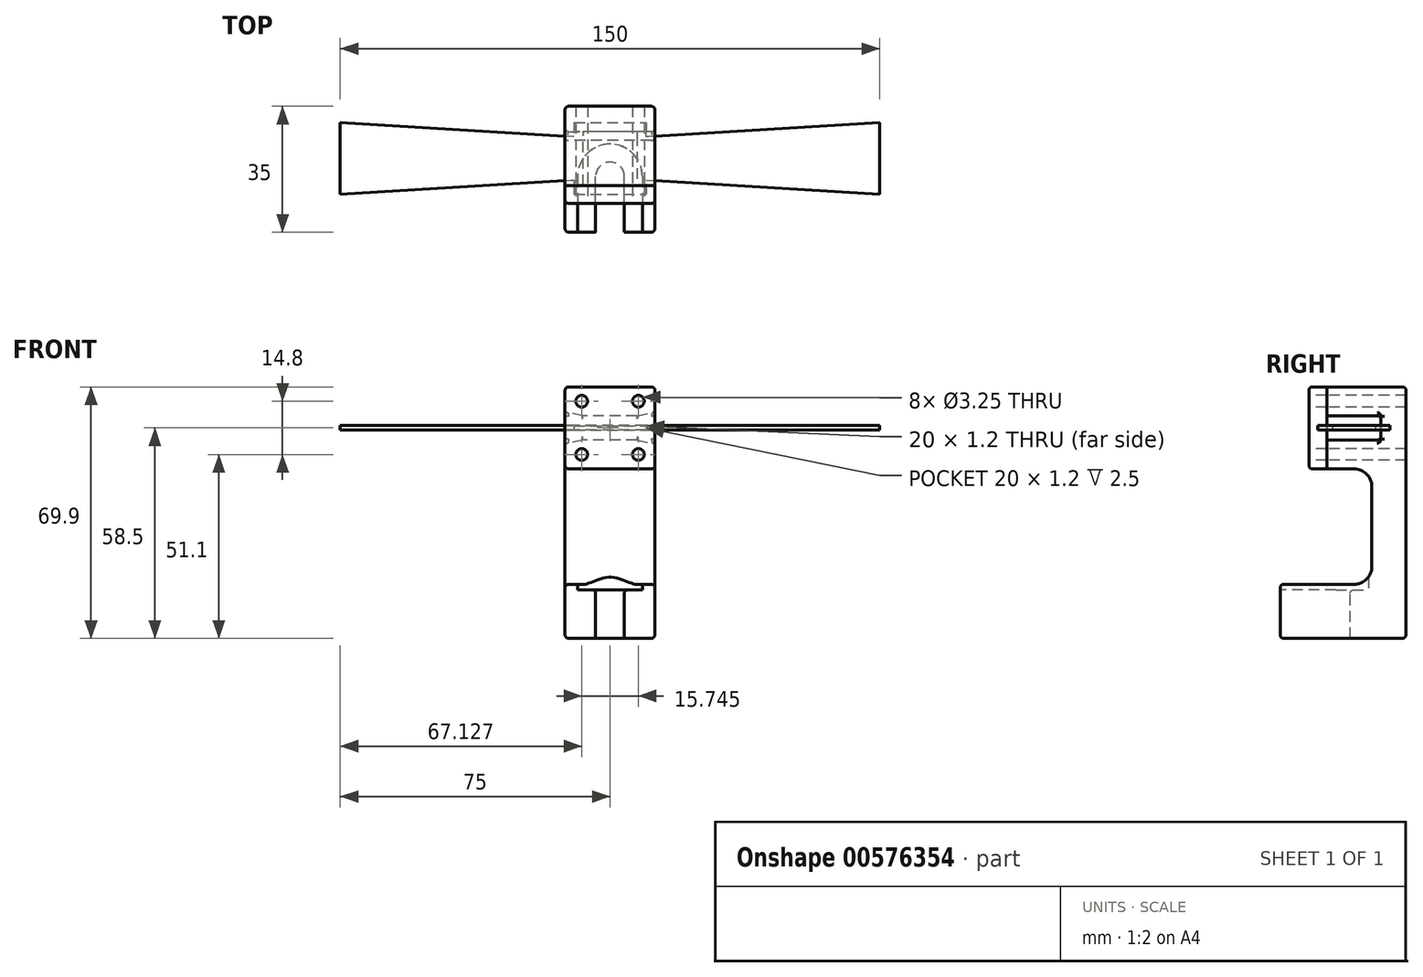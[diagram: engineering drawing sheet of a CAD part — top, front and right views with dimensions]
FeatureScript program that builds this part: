
annotation { "Feature Type Name" : "Feature", "Feature Type Description" : "" }
export const myFeature = defineFeature(function(context is Context, id is Id, definition is map)
    precondition{}
    {
        {
            var Q0;
            Q0=qCreatedBy(makeId("Top.planeOp"),FACE);
            var sketch = newSketch(context, id + "F0", { "sketchPlane" : qUnion([Q0])});
            skLineSegment(sketch, "E0", {"start": v(-142.1, 7.82) * mm, "end": v(142.1, -7.82) * mm, "construction": true});
            skLineSegment(sketch, "E1", {"start": v(-142.1, 0) * mm, "end": v(142.1, 0) * mm, "construction": true});
            skLineSegment(sketch, "E2", {"start": v(-142.1, -7.82) * mm, "end": v(142.1, 7.82) * mm, "construction": true});
            skLineSegment(sketch, "E3", {"start": v(-109.15, 10.59) * mm, "end": v(0, 4.58) * mm});
            skLineSegment(sketch, "E4", {"start": v(-109.15, 1.42) * mm, "end": v(-83.26, 0) * mm});
            skLineSegment(sketch, "E5", {"start": v(-109.15, -10.59) * mm, "end": v(0, -4.58) * mm});
            skLineSegment(sketch, "E6", {"start": v(109.15, 10.59) * mm, "end": v(0, 4.58) * mm});
            skLineSegment(sketch, "E7", {"start": v(0, 26.52) * mm, "end": v(0, -30.87) * mm, "construction": true});
            skLineSegment(sketch, "E8.trimOffspring", {"start": v(-83.26, 0) * mm, "end": v(-109.15, -1.42) * mm});
            skLineSegment(sketch, "E9.trimOffspring", {"start": v(0, -4.58) * mm, "end": v(109.15, -10.59) * mm});
            skLineSegment(sketch, "E10.trimOffspring", {"start": v(83.26, 0) * mm, "end": v(109.15, 1.42) * mm});
            skLineSegment(sketch, "E11.trimOffspring", {"start": v(83.26, 0) * mm, "end": v(109.15, -1.42) * mm});
            skLineSegment(sketch, "E12", {"start": v(109.15, 10.59) * mm, "end": v(109.15, 1.42) * mm});
            skLineSegment(sketch, "E13", {"start": v(109.15, -1.42) * mm, "end": v(109.15, -10.59) * mm});
            skLineSegment(sketch, "E14", {"start": v(-109.15, 10.59) * mm, "end": v(-109.15, 1.42) * mm});
            skLineSegment(sketch, "E15", {"start": v(-109.15, -1.42) * mm, "end": v(-109.15, -10.59) * mm});
            skSolve(sketch);
        }
        {
            var Q0;
            Q0=qCreatedBy(makeId("Right.planeOp"),FACE);
            var sketch = newSketch(context, id + "F1", { "sketchPlane" : qUnion([Q0])});
            skLineSegment(sketch, "E16", {"start": v(14.5, -58.5) * mm, "end": v(-20.5, -58.5) * mm});
            skLineSegment(sketch, "E17", {"start": v(14.5, 11.4) * mm, "end": v(-7.5, 11.4) * mm});
            skLineSegment(sketch, "E18", {"start": v(0, 18.84) * mm, "end": v(0, -56.33) * mm, "construction": true});
            skLineSegment(sketch, "E19.bottom", {"start": v(-7.5, 3.4) * mm, "end": v(7.5, 3.4) * mm});
            skLineSegment(sketch, "E19.right", {"start": v(7.5, 3.4) * mm, "end": v(7.5, -3.4) * mm});
            skLineSegment(sketch, "E20.top", {"start": v(-7.5, -3.4) * mm, "end": v(7.5, -3.4) * mm});
            skLineSegment(sketch, "E21", {"start": v(-7.5, -11.4) * mm, "end": v(5, -11.4) * mm});
            skLineSegment(sketch, "E22", {"start": v(5, -11.4) * mm, "end": v(5, -43.5) * mm});
            skLineSegment(sketch, "E23", {"start": v(5, -43.5) * mm, "end": v(-20.5, -43.5) * mm});
            skLineSegment(sketch, "E24.trimOffspring", {"start": v(-20.5, -43.5) * mm, "end": v(-20.5, -58.5) * mm});
            skLineSegment(sketch, "E25", {"start": v(14.5, 11.4) * mm, "end": v(14.5, -58.5) * mm});
            skLineSegment(sketch, "E26", {"start": v(-7.5, 11.4) * mm, "end": v(-7.5, 3.4) * mm});
            skLineSegment(sketch, "E27", {"start": v(-7.5, -3.4) * mm, "end": v(-7.5, -11.4) * mm});
            skLineSegment(sketch, "E28", {"start": v(-5, -34.47) * mm, "end": v(-5, -58.14) * mm, "construction": true});
            skSolve(sketch);
        }
        {
            var Q0;
            Q0 = qSketchRegion(id + "F1", true);
            extrude(context, id + "F2", {"entities" : qUnion([Q0]), "depth" : 25 * mm, "offsetDistance" : 25 * mm, "symmetric" : true});
        }
        {
            var Q0;
            Q0=makeQuery(id+"F2.opExtrude","SWEPT_FACE",FACE,{"disambiguationData":[OSD([sQuery(id+"F1.wireOp",EDGE,"E26")])]});
            var sketch = newSketch(context, id + "F3", { "sketchPlane" : qUnion([Q0])});
            skCircle(sketch, "E29", {"center": v(-7.87, 7.4) * mm, "radius": 1.25 * mm});
            skCircle(sketch, "E30", {"center": v(7.87, 7.4) * mm, "radius": 1.25 * mm});
            skCircle(sketch, "E31", {"center": v(-7.87, -7.4) * mm, "radius": 1.25 * mm});
            skCircle(sketch, "E32", {"center": v(7.87, -7.4) * mm, "radius": 1.25 * mm});
            skSolve(sketch);
        }
        {
            var Q0;
            Q0 = qSketchRegion(id + "F3", true);
            extrude(context, id + "F4", {"entities" : qUnion([Q0]), "operationType" : NewBodyOperationType.REMOVE, "oppositeDirection" : true, "depth" : 10 * mm, "offsetDistance" : 25 * mm});
        }
        {
            var Q0;
            Q0=qCreatedBy(makeId("Right.planeOp"),FACE);
            var sketch = newSketch(context, id + "F5", { "sketchPlane" : qUnion([Q0])});
            skLineSegment(sketch, "E33", {"start": v(-7.5, 11.4) * mm, "end": v(-12.5, 11.4) * mm});
            skLineSegment(sketch, "E34", {"start": v(-12.5, 11.4) * mm, "end": v(-12.5, -11.4) * mm});
            skLineSegment(sketch, "E35", {"start": v(-12.5, -11.4) * mm, "end": v(-7.5, -11.4) * mm});
            skLineSegment(sketch, "E36", {"start": v(-7.5, -11.4) * mm, "end": v(-7.5, 11.4) * mm});
            skSolve(sketch);
        }
        {
            var Q0;
            Q0 = qSketchRegion(id + "F5", true);
            extrude(context, id + "F6", {"entities" : qUnion([Q0]), "depth" : 25 * mm, "offsetDistance" : 25 * mm, "symmetric" : true});
        }
        {
            var Q0;
            Q0=makeQuery(id+"F6.opExtrude","SWEPT_FACE",FACE,{"disambiguationData":[OSD([sQuery(id+"F5.wireOp",EDGE,"E34")])]});
            var sketch = newSketch(context, id + "F7", { "sketchPlane" : qUnion([Q0])});
            skCircle(sketch, "E37", {"center": v(-7.87, 7.4) * mm, "radius": 1.63 * mm});
            skCircle(sketch, "E38", {"center": v(-7.87, -7.4) * mm, "radius": 1.63 * mm});
            skCircle(sketch, "E39", {"center": v(7.87, -7.4) * mm, "radius": 1.63 * mm});
            skCircle(sketch, "E40", {"center": v(7.87, 7.4) * mm, "radius": 1.63 * mm});
            skSolve(sketch);
        }
        {
            var Q0;
            Q0 = qSketchRegion(id + "F7", true);
            extrude(context, id + "F8", {"entities" : qUnion([Q0]), "operationType" : NewBodyOperationType.REMOVE, "endBound" : BoundingType.THROUGH_ALL, "oppositeDirection" : true, "depth" : 25 * mm, "offsetDistance" : 25 * mm});
        }
        {
            var Q0;
            Q0=qCreatedBy(makeId("Front.planeOp"),FACE);
            var sketch = newSketch(context, id + "F9", { "sketchPlane" : qUnion([Q0])});
            skLineSegment(sketch, "E41.bottom", {"start": v(-10, 0.6) * mm, "end": v(10, 0.6) * mm});
            skLineSegment(sketch, "E41.top", {"start": v(-10, -0.6) * mm, "end": v(10, -0.6) * mm});
            skLineSegment(sketch, "E41.left", {"start": v(-10, 0.6) * mm, "end": v(-10, -0.6) * mm});
            skLineSegment(sketch, "E41.right", {"start": v(10, 0.6) * mm, "end": v(10, -0.6) * mm});
            skSolve(sketch);
        }
        {
            var Q0;
            Q0 = qSketchRegion(id + "F9", true);
            extrude(context, id + "F10", {"entities" : qUnion([Q0]), "operationType" : NewBodyOperationType.REMOVE, "oppositeDirection" : true, "depth" : 20 * mm, "offsetDistance" : 25 * mm, "symmetric" : true});
        }
        {
            var Q0;
            Q0=makeQuery(id+"F2.opExtrude","CAP_EDGE",EDGE,{"disambiguationData":[OSD([sQuery(id+"F1.wireOp",EDGE,"E20.top")])],"isStart":true});
            var Q1;
            Q1=makeQuery(id+"F2.opExtrude","CAP_EDGE",EDGE,{"disambiguationData":[OSD([sQuery(id+"F1.wireOp",EDGE,"E19.bottom")])],"isStart":true});
            var Q2;
            Q2=makeQuery(id+"F2.opExtrude","CAP_EDGE",EDGE,{"disambiguationData":[OSD([sQuery(id+"F1.wireOp",EDGE,"E20.top")])],"isStart":false});
            var Q3;
            Q3=makeQuery(id+"F2.opExtrude","CAP_EDGE",EDGE,{"disambiguationData":[OSD([sQuery(id+"F1.wireOp",EDGE,"E19.bottom")])],"isStart":false});
            chamfer(context, id + "F11", {"entities" : qUnion([Q0, Q1, Q2, Q3]), "chamferType" : ChamferType.TWO_OFFSETS, "width1" : 1 * mm, "oppositeDirection" : false, "width2" : 5 * mm, "tangentPropagation" : true});
        }
        {
            var Q0;
            Q0=makeQuery(id+"F2.opExtrude","SWEPT_EDGE",EDGE,{"disambiguationData":[OSD([sQuery(id+"F1.wireOp",EDGE,"E22"),sQuery(id+"F1.wireOp",EDGE,"E23")])]});
            var Q1;
            Q1=makeQuery(id+"F2.opExtrude","SWEPT_EDGE",EDGE,{"disambiguationData":[OSD([sQuery(id+"F1.wireOp",EDGE,"E21"),sQuery(id+"F1.wireOp",EDGE,"E22")])]});
            fillet(context, id + "F12", {"entities" : qUnion([Q0, Q1]), "radius" : 5 * mm, "tangentPropagation" : true, "allowEdgeOverflow" : false});
        }
        {
            var Q0;
            Q0=makeQuery(id+"F2.opExtrude","SWEPT_FACE",FACE,{"disambiguationData":[OSD([sQuery(id+"F1.wireOp",EDGE,"E23")])]});
            var sketch = newSketch(context, id + "F13", { "sketchPlane" : qUnion([Q0])});
            skArc(sketch, "E42", {"start": v(4, -5) * mm, "mid": v(0, -1) * mm, "end": v(-4, -5) * mm});
            skLineSegment(sketch, "E43", {"start": v(-4, -5) * mm, "end": v(-4, -20.5) * mm});
            skLineSegment(sketch, "E44", {"start": v(4, -5) * mm, "end": v(4, -20.5) * mm});
            skLineSegment(sketch, "E45", {"start": v(4, -20.5) * mm, "end": v(-4, -20.5) * mm});
            skSolve(sketch);
        }
        {
            var Q0;
            Q0 = qSketchRegion(id + "F13", true);
            extrude(context, id + "F14", {"entities" : qUnion([Q0]), "operationType" : NewBodyOperationType.REMOVE, "endBound" : BoundingType.THROUGH_ALL, "oppositeDirection" : true, "depth" : 25 * mm, "offsetDistance" : 25 * mm});
        }
        {
            var Q0;
            Q0=makeQuery(id+"F2.opExtrude","SWEPT_FACE",FACE,{"disambiguationData":[OSD([sQuery(id+"F1.wireOp",EDGE,"E23")])]});
            cPlane(context, id + "F15", {"entities" : qUnion([Q0]), "cplaneType" : CPlaneType.OFFSET, "offset" : 1.5 * mm, "oppositeDirection" : true, "width" : 150 * mm, "height" : 150 * mm});
        }
        {
            var Q0;
            Q0=qCreatedBy(id+"F15.planeOp",FACE);
            var sketch = newSketch(context, id + "F16", { "sketchPlane" : qUnion([Q0])});
            skArc(sketch, "E46", {"start": v(9, -5) * mm, "mid": v(0, 4) * mm, "end": v(-9, -5) * mm});
            skLineSegment(sketch, "E47", {"start": v(-9, -5) * mm, "end": v(-9, -20.5) * mm});
            skLineSegment(sketch, "E48", {"start": v(9, -5) * mm, "end": v(9, -20.5) * mm});
            skLineSegment(sketch, "E49", {"start": v(9, -20.5) * mm, "end": v(-9, -20.5) * mm});
            skSolve(sketch);
        }
        {
            var Q0;
            Q0 = qSketchRegion(id + "F16", true);
            extrude(context, id + "F17", {"entities" : qUnion([Q0]), "operationType" : NewBodyOperationType.REMOVE, "depth" : 10 * mm, "offsetDistance" : 25 * mm});
        }
        {
            var Q0;
            Q0=makeQuery(id+"F2.opExtrude","SWEPT_EDGE",EDGE,{"disambiguationData":[OSD([sQuery(id+"F1.wireOp",EDGE,"E23"),sQuery(id+"F1.wireOp",EDGE,"E24.trimOffspring")])]});
            var Q1;
            Q1=makeQuery(id+"F2.opExtrude","SWEPT_EDGE",EDGE,{"disambiguationData":[OSD([sQuery(id+"F1.wireOp",EDGE,"E17"),sQuery(id+"F1.wireOp",EDGE,"E25")])]});
            var Q2;
            Q2=makeQuery(id+"F2.opExtrude","SWEPT_EDGE",EDGE,{"disambiguationData":[OSD([sQuery(id+"F1.wireOp",EDGE,"E16"),sQuery(id+"F1.wireOp",EDGE,"E25")])]});
            var Q3;
            Q3=makeQuery(id+"F2.opExtrude","SWEPT_EDGE",EDGE,{"disambiguationData":[OSD([sQuery(id+"F1.wireOp",EDGE,"E16"),sQuery(id+"F1.wireOp",EDGE,"E24.trimOffspring")])]});
            var Q4;
            Q4=makeQuery(id+"F6.opExtrude","SWEPT_EDGE",EDGE,{"disambiguationData":[OSD([sQuery(id+"F5.wireOp",EDGE,"E34"),sQuery(id+"F5.wireOp",EDGE,"E35")])]});
            var Q5;
            Q5=makeQuery(id+"F6.opExtrude","SWEPT_EDGE",EDGE,{"disambiguationData":[OSD([sQuery(id+"F5.wireOp",EDGE,"E33"),sQuery(id+"F5.wireOp",EDGE,"E34")])]});
            fillet(context, id + "F18", {"entities" : qUnion([Q0, Q1, Q2, Q3, Q4, Q5]), "radius" : 1 * mm, "tangentPropagation" : true, "allowEdgeOverflow" : false});
        }
        {
            var Q0;
            Q0=makeQuery(id+"F2.opExtrude","SWEPT_EDGE",EDGE,{"disambiguationData":[OSD([sQuery(id+"F1.wireOp",EDGE,"E19.bottom"),sQuery(id+"F1.wireOp",EDGE,"E19.right")])]});
            var Q1;
            Q1=makeQuery(id+"F11.opChamfer","BLEND_EDGE",EDGE,{"blendedFrom":[makeQuery(id+"F2.opExtrude","CAP_EDGE",EDGE,{"disambiguationData":[OSD([sQuery(id+"F1.wireOp",EDGE,"E19.bottom")])],"isStart":true}),makeQuery(id+"F2.opExtrude","SWEPT_FACE",FACE,{"disambiguationData":[OSD([sQuery(id+"F1.wireOp",EDGE,"E19.right")])]})],"blendedInto":[makeQuery(id+"F2.opExtrude","SWEPT_FACE",FACE,{"disambiguationData":[OSD([sQuery(id+"F1.wireOp",EDGE,"E19.right")])]})]});
            var Q2;
            Q2=makeQuery(id+"F11.opChamfer","BLEND_EDGE",EDGE,{"blendedFrom":[makeQuery(id+"F2.opExtrude","CAP_EDGE",EDGE,{"disambiguationData":[OSD([sQuery(id+"F1.wireOp",EDGE,"E20.top")])],"isStart":true}),makeQuery(id+"F2.opExtrude","SWEPT_FACE",FACE,{"disambiguationData":[OSD([sQuery(id+"F1.wireOp",EDGE,"E19.right")])]})],"blendedInto":[makeQuery(id+"F2.opExtrude","SWEPT_FACE",FACE,{"disambiguationData":[OSD([sQuery(id+"F1.wireOp",EDGE,"E19.right")])]})]});
            var Q3;
            Q3=makeQuery(id+"F2.opExtrude","SWEPT_EDGE",EDGE,{"disambiguationData":[OSD([sQuery(id+"F1.wireOp",EDGE,"E19.right"),sQuery(id+"F1.wireOp",EDGE,"E20.top")])]});
            var Q4;
            Q4=makeQuery(id+"F11.opChamfer","BLEND_EDGE",EDGE,{"blendedFrom":[makeQuery(id+"F2.opExtrude","CAP_EDGE",EDGE,{"disambiguationData":[OSD([sQuery(id+"F1.wireOp",EDGE,"E20.top")])],"isStart":false}),makeQuery(id+"F2.opExtrude","SWEPT_FACE",FACE,{"disambiguationData":[OSD([sQuery(id+"F1.wireOp",EDGE,"E19.right")])]})],"blendedInto":[makeQuery(id+"F2.opExtrude","SWEPT_FACE",FACE,{"disambiguationData":[OSD([sQuery(id+"F1.wireOp",EDGE,"E19.right")])]})]});
            var Q5;
            Q5=makeQuery(id+"F11.opChamfer","BLEND_EDGE",EDGE,{"blendedFrom":[makeQuery(id+"F2.opExtrude","CAP_EDGE",EDGE,{"disambiguationData":[OSD([sQuery(id+"F1.wireOp",EDGE,"E19.bottom")])],"isStart":false}),makeQuery(id+"F2.opExtrude","SWEPT_FACE",FACE,{"disambiguationData":[OSD([sQuery(id+"F1.wireOp",EDGE,"E19.right")])]})],"blendedInto":[makeQuery(id+"F2.opExtrude","SWEPT_FACE",FACE,{"disambiguationData":[OSD([sQuery(id+"F1.wireOp",EDGE,"E19.right")])]})]});
            fillet(context, id + "F19", {"entities" : qUnion([Q0, Q1, Q2, Q3, Q4, Q5]), "radius" : 1 * mm, "tangentPropagation" : true, "allowEdgeOverflow" : false});
        }
        {
            var Q0;
            {var subQ0=sQuery(id+"F1.wireOp",EDGE,"E19.bottom");Q0=makeQuery(id+"F11.opChamfer","BLEND_EDGE",EDGE,{"blendedFrom":[makeQuery(id+"F2.opExtrude","CAP_EDGE",EDGE,{"disambiguationData":[OSD([subQ0])],"isStart":true}),makeQuery(id+"F2.opExtrude","CAP_FACE",FACE,{"disambiguationData":[OSD([sQuery(id+"F1.wireOp",EDGE,"E16"),sQuery(id+"F1.wireOp",EDGE,"E17"),subQ0,sQuery(id+"F1.wireOp",EDGE,"E19.right"),sQuery(id+"F1.wireOp",EDGE,"E20.top"),sQuery(id+"F1.wireOp",EDGE,"E21"),sQuery(id+"F1.wireOp",EDGE,"E22"),sQuery(id+"F1.wireOp",EDGE,"E23"),sQuery(id+"F1.wireOp",EDGE,"E24.trimOffspring"),sQuery(id+"F1.wireOp",EDGE,"E25"),sQuery(id+"F1.wireOp",EDGE,"E26"),sQuery(id+"F1.wireOp",EDGE,"E27")])],"isStart":true})],"blendedInto":[makeQuery(id+"F2.opExtrude","CAP_FACE",FACE,{"disambiguationData":[OSD([sQuery(id+"F1.wireOp",EDGE,"E16"),sQuery(id+"F1.wireOp",EDGE,"E17"),subQ0,sQuery(id+"F1.wireOp",EDGE,"E19.right"),sQuery(id+"F1.wireOp",EDGE,"E20.top"),sQuery(id+"F1.wireOp",EDGE,"E21"),sQuery(id+"F1.wireOp",EDGE,"E22"),sQuery(id+"F1.wireOp",EDGE,"E23"),sQuery(id+"F1.wireOp",EDGE,"E24.trimOffspring"),sQuery(id+"F1.wireOp",EDGE,"E25"),sQuery(id+"F1.wireOp",EDGE,"E26"),sQuery(id+"F1.wireOp",EDGE,"E27")])],"isStart":true})]});}
            var Q1;
            Q1=makeQuery(id+"F2.opExtrude","CAP_EDGE",EDGE,{"disambiguationData":[OSD([sQuery(id+"F1.wireOp",EDGE,"E17")])],"isStart":true});
            var Q2;
            Q2=makeQuery(id+"F2.opExtrude","CAP_EDGE",EDGE,{"disambiguationData":[OSD([sQuery(id+"F1.wireOp",EDGE,"E17")])],"isStart":false});
            var Q3;
            {var subQ0=sQuery(id+"F1.wireOp",EDGE,"E19.bottom");Q3=makeQuery(id+"F11.opChamfer","BLEND_EDGE",EDGE,{"blendedFrom":[makeQuery(id+"F2.opExtrude","CAP_EDGE",EDGE,{"disambiguationData":[OSD([subQ0])],"isStart":false}),makeQuery(id+"F2.opExtrude","CAP_FACE",FACE,{"disambiguationData":[OSD([sQuery(id+"F1.wireOp",EDGE,"E16"),sQuery(id+"F1.wireOp",EDGE,"E17"),subQ0,sQuery(id+"F1.wireOp",EDGE,"E19.right"),sQuery(id+"F1.wireOp",EDGE,"E20.top"),sQuery(id+"F1.wireOp",EDGE,"E21"),sQuery(id+"F1.wireOp",EDGE,"E22"),sQuery(id+"F1.wireOp",EDGE,"E23"),sQuery(id+"F1.wireOp",EDGE,"E24.trimOffspring"),sQuery(id+"F1.wireOp",EDGE,"E25"),sQuery(id+"F1.wireOp",EDGE,"E26"),sQuery(id+"F1.wireOp",EDGE,"E27")])],"isStart":false})],"blendedInto":[makeQuery(id+"F2.opExtrude","CAP_FACE",FACE,{"disambiguationData":[OSD([sQuery(id+"F1.wireOp",EDGE,"E16"),sQuery(id+"F1.wireOp",EDGE,"E17"),subQ0,sQuery(id+"F1.wireOp",EDGE,"E19.right"),sQuery(id+"F1.wireOp",EDGE,"E20.top"),sQuery(id+"F1.wireOp",EDGE,"E21"),sQuery(id+"F1.wireOp",EDGE,"E22"),sQuery(id+"F1.wireOp",EDGE,"E23"),sQuery(id+"F1.wireOp",EDGE,"E24.trimOffspring"),sQuery(id+"F1.wireOp",EDGE,"E25"),sQuery(id+"F1.wireOp",EDGE,"E26"),sQuery(id+"F1.wireOp",EDGE,"E27")])],"isStart":false})]});}
            var Q4;
            Q4=makeQuery(id+"F6.opExtrude","CAP_EDGE",EDGE,{"disambiguationData":[OSD([sQuery(id+"F5.wireOp",EDGE,"E33")])],"isStart":true});
            var Q5;
            Q5=makeQuery(id+"F6.opExtrude","CAP_EDGE",EDGE,{"disambiguationData":[OSD([sQuery(id+"F5.wireOp",EDGE,"E33")])],"isStart":false});
            var Q6;
            Q6=makeQuery(id+"F14.boolean.opBoolean","COPY",EDGE,{"derivedFrom":makeQuery(id+"F14.opExtrude","SWEPT_EDGE",EDGE,{"disambiguationData":[OSD([sQuery(id+"F1.wireOp",EDGE,"E23"),sQuery(id+"F1.wireOp",EDGE,"E24.trimOffspring"),sQuery(id+"F13.wireOp",EDGE,"E43"),sQuery(id+"F13.wireOp",EDGE,"E45")])]})});
            var Q7;
            {var subQ0=sQuery(id+"F16.wireOp",EDGE,"E49");Q7=makeQuery(id+"F17.boolean.opBoolean","COPY",EDGE,{"disambiguationData":[TD([makeQuery(id+"F14.boolean.opBoolean","COPY",FACE,{"derivedFrom":makeQuery(id+"F14.opExtrude","SWEPT_FACE",FACE,{"disambiguationData":[OSD([sQuery(id+"F13.wireOp",EDGE,"E44")])]})})])],"derivedFrom":makeQuery(id+"F17.opExtrude","CAP_EDGE",EDGE,{"disambiguationData":[OSD([subQ0])],"isStart":true})});}
            var Q8;
            {var subQ1=sQuery(id+"F16.wireOp",EDGE,"E49");Q8=makeQuery(id+"F17.boolean.opBoolean","COPY",EDGE,{"disambiguationData":[TD([makeQuery(id+"F14.boolean.opBoolean","COPY",FACE,{"derivedFrom":makeQuery(id+"F14.opExtrude","SWEPT_FACE",FACE,{"disambiguationData":[OSD([sQuery(id+"F13.wireOp",EDGE,"E43")])]})})])],"derivedFrom":makeQuery(id+"F17.opExtrude","CAP_EDGE",EDGE,{"disambiguationData":[OSD([subQ1])],"isStart":true})});}
            var Q9;
            Q9=makeQuery(id+"F17.boolean.opBoolean","COPY",EDGE,{"derivedFrom":makeQuery(id+"F17.opExtrude","SWEPT_EDGE",EDGE,{"disambiguationData":[OSD([sQuery(id+"F16.wireOp",EDGE,"E48"),sQuery(id+"F16.wireOp",EDGE,"E49")])]})});
            var Q10;
            Q10=makeQuery(id+"F17.boolean.opBoolean","INTERSECT",EDGE,{"derivedFrom":[makeQuery(id+"F14.boolean.opBoolean","COPY",FACE,{"derivedFrom":makeQuery(id+"F14.opExtrude","SWEPT_FACE",FACE,{"disambiguationData":[OSD([sQuery(id+"F13.wireOp",EDGE,"E42")])]})}),makeQuery(id+"F17.opExtrude","CAP_FACE",FACE,{"disambiguationData":[OSD([sQuery(id+"F16.wireOp",EDGE,"E46"),sQuery(id+"F16.wireOp",EDGE,"E47"),sQuery(id+"F16.wireOp",EDGE,"E48"),sQuery(id+"F16.wireOp",EDGE,"E49")])],"isStart":true})]});
            fillet(context, id + "F20", {"entities" : qUnion([Q0, Q1, Q2, Q3, Q4, Q5, Q6, Q7, Q8, Q9, Q10]), "radius" : 1 * mm, "tangentPropagation" : true, "allowEdgeOverflow" : false});
        }
        {
            var Q0;
            Q0=qCreatedBy(makeId("Top.planeOp"),FACE);
            var sketch = newSketch(context, id + "F21", { "sketchPlane" : qUnion([Q0])});
            skLineSegment(sketch, "E50", {"start": v(10, 10) * mm, "end": v(-10, 10) * mm});
            skLineSegment(sketch, "E51", {"start": v(-10, 10) * mm, "end": v(-10, 6) * mm});
            skLineSegment(sketch, "E52", {"start": v(-10, 6) * mm, "end": v(-75, 10) * mm});
            skLineSegment(sketch, "E53", {"start": v(-75, 10) * mm, "end": v(-75, -10) * mm});
            skLineSegment(sketch, "E54", {"start": v(-75, -10) * mm, "end": v(-10, -6) * mm});
            skLineSegment(sketch, "E55", {"start": v(-10, -6) * mm, "end": v(-10, -10) * mm});
            skLineSegment(sketch, "E56", {"start": v(-10, -10) * mm, "end": v(10, -10) * mm});
            skLineSegment(sketch, "E57", {"start": v(10, -10) * mm, "end": v(10, -6) * mm});
            skLineSegment(sketch, "E58", {"start": v(10, -6) * mm, "end": v(75, -10) * mm});
            skLineSegment(sketch, "E59", {"start": v(75, -10) * mm, "end": v(75, 10) * mm});
            skLineSegment(sketch, "E60", {"start": v(75, 10) * mm, "end": v(10, 6) * mm});
            skLineSegment(sketch, "E61", {"start": v(10, 6) * mm, "end": v(10, 10) * mm});
            skSolve(sketch);
        }
        {
            var Q0;
            Q0 = qSketchRegion(id + "F21", true);
            extrude(context, id + "F22", {"entities" : qUnion([Q0]), "depth" : 1.25 * mm, "offsetDistance" : 25 * mm, "symmetric" : true});
        }
    });
